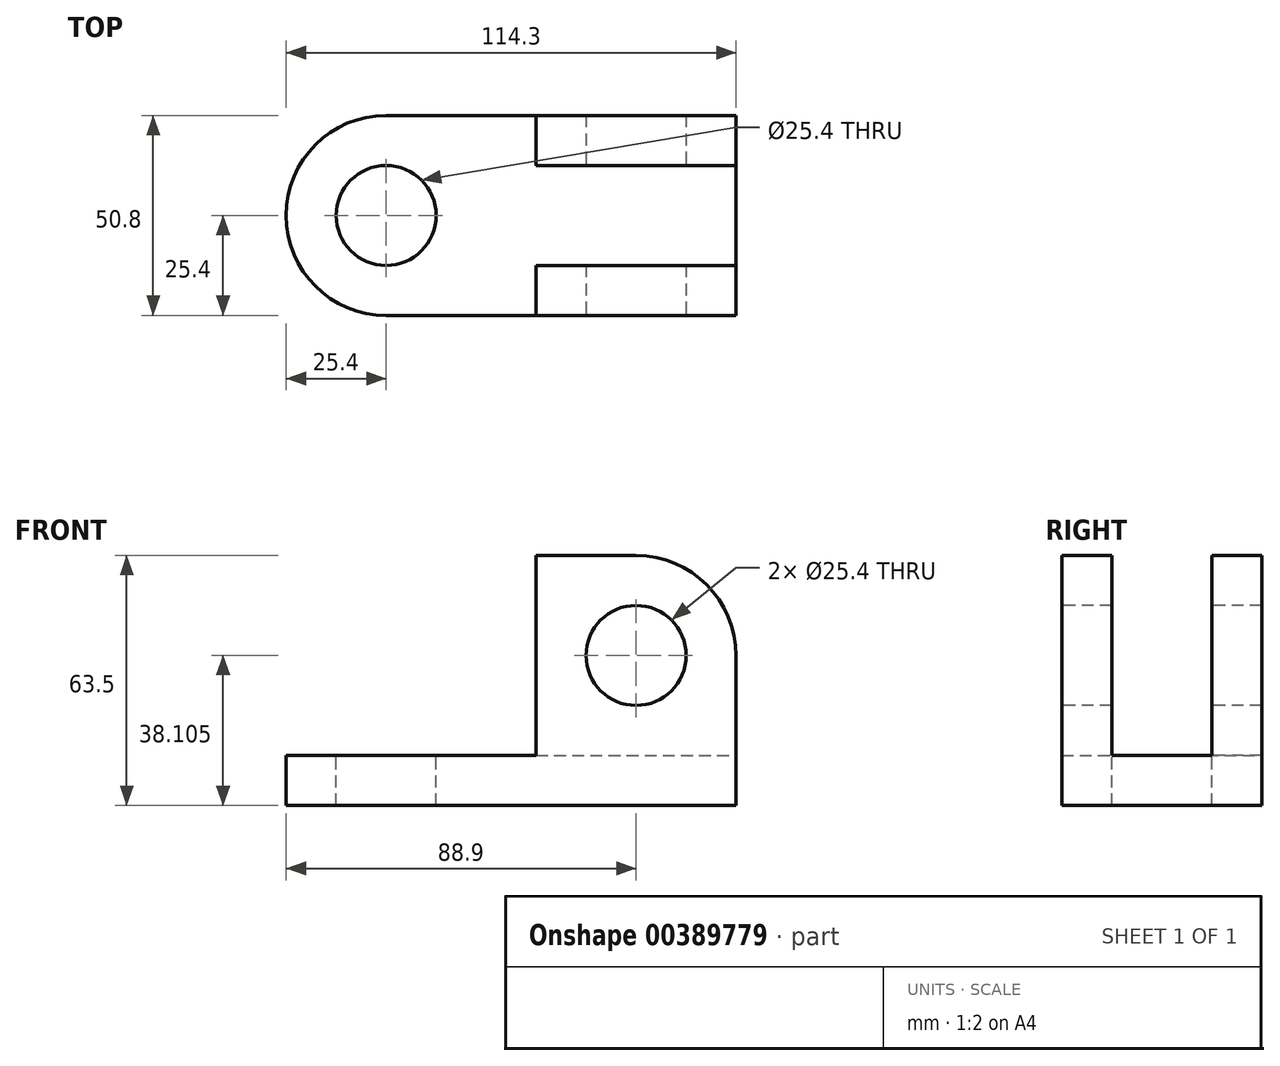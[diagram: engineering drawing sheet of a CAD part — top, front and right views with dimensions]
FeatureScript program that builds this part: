
annotation { "Feature Type Name" : "Feature", "Feature Type Description" : "" }
export const myFeature = defineFeature(function(context is Context, id is Id, definition is map)
    precondition{}
    {
        {
            var Q0;
            Q0=qCreatedBy(makeId("Front.planeOp"),FACE);
            var sketch = newSketch(context, id + "F0", { "sketchPlane" : qUnion([Q0])});
            skLineSegment(sketch, "E0.bottom", {"start": v(-51.63, 52.2) * mm, "end": v(62.67, 52.2) * mm});
            skLineSegment(sketch, "E0.top", {"start": v(-51.63, -11.3) * mm, "end": v(62.67, -11.3) * mm});
            skLineSegment(sketch, "E0.left", {"start": v(-51.63, 52.2) * mm, "end": v(-51.63, -11.3) * mm});
            skLineSegment(sketch, "E0.right", {"start": v(62.67, 52.2) * mm, "end": v(62.67, -11.3) * mm});
            skSolve(sketch);
        }
        {
            var Q0;
            Q0 = qSketchRegion(id + "F0", true);
            extrude(context, id + "F1", {"entities" : qUnion([Q0]), "depth" : 50.8 * mm});
        }
        {
            var Q0;
            Q0=makeQuery(id+"F1.opExtrude","SWEPT_FACE",FACE,{"disambiguationData":[OSD([sQuery(id+"F0.wireOp",EDGE,"E0.right")])]});
            var sketch = newSketch(context, id + "F2", { "sketchPlane" : qUnion([Q0])});
            skLineSegment(sketch, "E1.bottom", {"start": v(-38.1, 58.44) * mm, "end": v(-12.7, 58.44) * mm});
            skLineSegment(sketch, "E1.top", {"start": v(-38.1, 1.4) * mm, "end": v(-12.7, 1.4) * mm});
            skLineSegment(sketch, "E1.left", {"start": v(-38.1, 58.44) * mm, "end": v(-38.1, 1.4) * mm});
            skLineSegment(sketch, "E1.right", {"start": v(-12.7, 58.44) * mm, "end": v(-12.7, 1.4) * mm});
            skSolve(sketch);
        }
        {
            var Q0;
            Q0 = qSketchRegion(id + "F2", true);
            extrude(context, id + "F3", {"entities" : qUnion([Q0]), "operationType" : NewBodyOperationType.REMOVE, "endBound" : BoundingType.THROUGH_ALL, "oppositeDirection" : true, "depth" : 25.4 * mm});
        }
        {
            var Q0;
            {var subQ2=sQuery(id+"F0.wireOp",EDGE,"E0.bottom");Q0=makeQuery(id+"F3.boolean.opBoolean","SPLIT",FACE,{"disambiguationData":[TD([makeQuery(id+"F3.opExtrude","SWEPT_FACE",FACE,{"disambiguationData":[OSD([sQuery(id+"F2.wireOp",EDGE,"E1.left")])]})])],"derivedFrom":makeQuery(id+"F1.opExtrude","SWEPT_FACE",FACE,{"disambiguationData":[OSD([subQ2])]})});}
            var sketch = newSketch(context, id + "F4", { "sketchPlane" : qUnion([Q0])});
            skLineSegment(sketch, "E2.bottom", {"start": v(-51.63, -50.8) * mm, "end": v(11.87, -50.8) * mm});
            skLineSegment(sketch, "E2.top", {"start": v(-51.63, -38.1) * mm, "end": v(11.87, -38.1) * mm});
            skLineSegment(sketch, "E2.left", {"start": v(-51.63, -50.8) * mm, "end": v(-51.63, -38.1) * mm});
            skLineSegment(sketch, "E2.right", {"start": v(11.87, -50.8) * mm, "end": v(11.87, -38.1) * mm});
            skSolve(sketch);
        }
        {
            var Q0;
            Q0 = qSketchRegion(id + "F4", true);
            extrude(context, id + "F5", {"entities" : qUnion([Q0]), "operationType" : NewBodyOperationType.REMOVE, "oppositeDirection" : true, "depth" : 50.8 * mm});
        }
        {
            var Q0;
            {var subQ2=sQuery(id+"F0.wireOp",EDGE,"E0.bottom");Q0=makeQuery(id+"F3.boolean.opBoolean","SPLIT",FACE,{"disambiguationData":[TD([makeQuery(id+"F3.opExtrude","SWEPT_FACE",FACE,{"disambiguationData":[OSD([sQuery(id+"F2.wireOp",EDGE,"E1.right")])]})])],"derivedFrom":makeQuery(id+"F1.opExtrude","SWEPT_FACE",FACE,{"disambiguationData":[OSD([subQ2])]})});}
            var sketch = newSketch(context, id + "F6", { "sketchPlane" : qUnion([Q0])});
            skLineSegment(sketch, "E3.bottom", {"start": v(-51.63, 0) * mm, "end": v(11.87, 0) * mm});
            skLineSegment(sketch, "E3.top", {"start": v(-51.63, -12.7) * mm, "end": v(11.87, -12.7) * mm});
            skLineSegment(sketch, "E3.left", {"start": v(-51.63, 0) * mm, "end": v(-51.63, -12.7) * mm});
            skLineSegment(sketch, "E3.right", {"start": v(11.87, 0) * mm, "end": v(11.87, -12.7) * mm});
            skSolve(sketch);
        }
        {
            var Q0;
            Q0 = qSketchRegion(id + "F6", true);
            extrude(context, id + "F7", {"entities" : qUnion([Q0]), "operationType" : NewBodyOperationType.REMOVE, "oppositeDirection" : true, "depth" : 50.8 * mm});
        }
        {
            var Q0;
            Q0=makeQuery(id+"F1.opExtrude","CAP_FACE",FACE,{"disambiguationData":[OSD([sQuery(id+"F0.wireOp",EDGE,"E0.bottom"),sQuery(id+"F0.wireOp",EDGE,"E0.top"),sQuery(id+"F0.wireOp",EDGE,"E0.left"),sQuery(id+"F0.wireOp",EDGE,"E0.right")])],"isStart":false});
            var sketch = newSketch(context, id + "F8", { "sketchPlane" : qUnion([Q0])});
            skCircle(sketch, "E4", {"center": v(37.27, 26.8) * mm, "radius": 12.7 * mm});
            skPoint(sketch, "E4.centerSnap0", {"position": v(37.27, 52.2) * mm});
            skSolve(sketch);
        }
        {
            var Q0;
            Q0 = qSketchRegion(id + "F8", true);
            extrude(context, id + "F9", {"entities" : qUnion([Q0]), "operationType" : NewBodyOperationType.REMOVE, "endBound" : BoundingType.THROUGH_ALL, "oppositeDirection" : true, "depth" : 25.4 * mm});
        }
        {
            var Q0;
            {var subQ0=sQuery(id+"F0.wireOp",EDGE,"E0.bottom");var subQ1=sQuery(id+"F0.wireOp",EDGE,"E0.right");Q0=makeQuery(id+"F3.boolean.opBoolean","SPLIT",EDGE,{"disambiguationData":[TD([makeQuery(id+"F3.opExtrude","SWEPT_FACE",FACE,{"disambiguationData":[OSD([sQuery(id+"F2.wireOp",EDGE,"E1.left")])]})])],"derivedFrom":makeQuery(id+"F1.opExtrude","SWEPT_EDGE",EDGE,{"disambiguationData":[OSD([subQ0,subQ1])]})});}
            var Q1;
            Q1=makeQuery(id+"F5.boolean.opBoolean","COPY",EDGE,{"derivedFrom":makeQuery(id+"F5.opExtrude","CAP_EDGE",EDGE,{"disambiguationData":[OSD([sQuery(id+"F4.wireOp",EDGE,"E2.right")])],"isStart":true})});
            var Q2;
            Q2=makeQuery(id+"F7.boolean.opBoolean","COPY",EDGE,{"derivedFrom":makeQuery(id+"F7.opExtrude","CAP_EDGE",EDGE,{"disambiguationData":[OSD([sQuery(id+"F6.wireOp",EDGE,"E3.right")])],"isStart":true})});
            var Q3;
            {var subQ0=sQuery(id+"F0.wireOp",EDGE,"E0.bottom");var subQ1=sQuery(id+"F0.wireOp",EDGE,"E0.right");Q3=makeQuery(id+"F3.boolean.opBoolean","SPLIT",EDGE,{"disambiguationData":[TD([makeQuery(id+"F3.opExtrude","SWEPT_FACE",FACE,{"disambiguationData":[OSD([sQuery(id+"F2.wireOp",EDGE,"E1.right")])]})])],"derivedFrom":makeQuery(id+"F1.opExtrude","SWEPT_EDGE",EDGE,{"disambiguationData":[OSD([subQ0,subQ1])]})});}
            var Q4;
            Q4=makeQuery(id+"F1.opExtrude","CAP_EDGE",EDGE,{"disambiguationData":[OSD([sQuery(id+"F0.wireOp",EDGE,"E0.left")])],"isStart":false});
            var Q5;
            Q5=makeQuery(id+"F1.opExtrude","CAP_EDGE",EDGE,{"disambiguationData":[OSD([sQuery(id+"F0.wireOp",EDGE,"E0.left")])],"isStart":true});
            fillet(context, id + "F10", {"entities" : qUnion([Q0, Q1, Q2, Q3, Q4, Q5]), "radius" : 25.4 * mm, "tangentPropagation" : true, "allowEdgeOverflow" : false});
        }
        {
            var Q0;
            Q0=makeQuery(id+"F7.boolean.opBoolean","MERGE",FACE,{"derivedFrom":[makeQuery(id+"F5.boolean.opBoolean","MERGE",FACE,{"derivedFrom":[makeQuery(id+"F3.boolean.opBoolean","COPY",FACE,{"derivedFrom":makeQuery(id+"F3.opExtrude","SWEPT_FACE",FACE,{"disambiguationData":[OSD([sQuery(id+"F2.wireOp",EDGE,"E1.top")])]})}),makeQuery(id+"F5.opExtrude","CAP_FACE",FACE,{"disambiguationData":[OSD([sQuery(id+"F4.wireOp",EDGE,"E2.bottom"),sQuery(id+"F4.wireOp",EDGE,"E2.top"),sQuery(id+"F4.wireOp",EDGE,"E2.left"),sQuery(id+"F4.wireOp",EDGE,"E2.right")])],"isStart":false})]}),makeQuery(id+"F7.opExtrude","CAP_FACE",FACE,{"disambiguationData":[OSD([sQuery(id+"F6.wireOp",EDGE,"E3.bottom"),sQuery(id+"F6.wireOp",EDGE,"E3.top"),sQuery(id+"F6.wireOp",EDGE,"E3.left"),sQuery(id+"F6.wireOp",EDGE,"E3.right")])],"isStart":false})]});
            var sketch = newSketch(context, id + "F11", { "sketchPlane" : qUnion([Q0])});
            skCircle(sketch, "E5", {"center": v(-26.23, -25.4) * mm, "radius": 12.7 * mm});
            skPoint(sketch, "E5.centerSnap0", {"position": v(-51.63, -25.4) * mm});
            skSolve(sketch);
        }
        {
            var Q0;
            Q0 = qSketchRegion(id + "F11", true);
            extrude(context, id + "F12", {"entities" : qUnion([Q0]), "operationType" : NewBodyOperationType.REMOVE, "endBound" : BoundingType.THROUGH_ALL, "oppositeDirection" : true, "depth" : 25.4 * mm});
        }
    });
